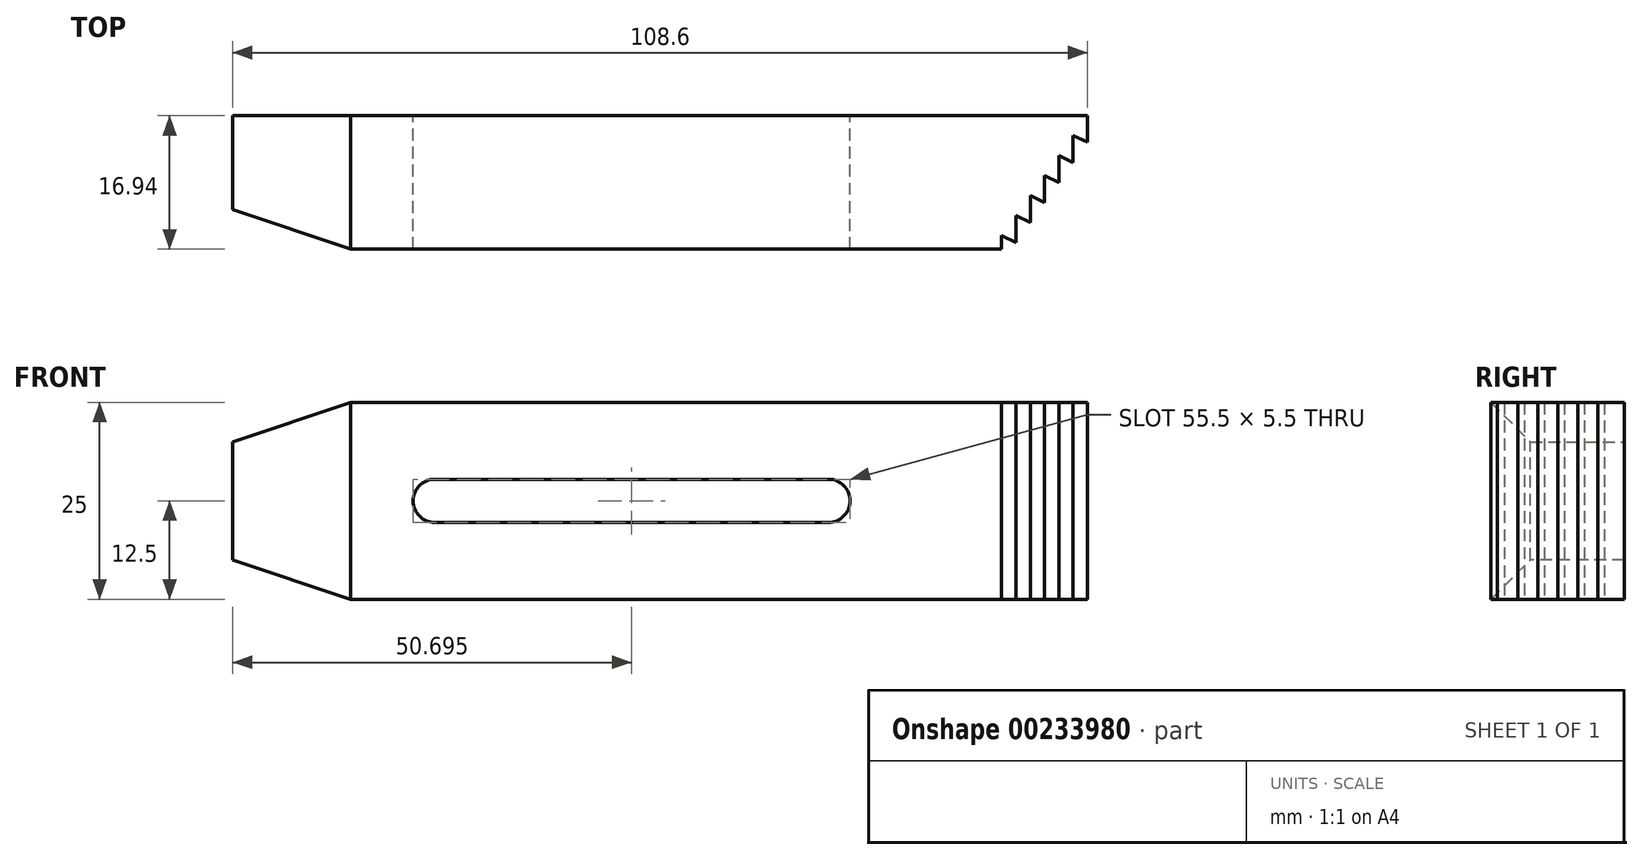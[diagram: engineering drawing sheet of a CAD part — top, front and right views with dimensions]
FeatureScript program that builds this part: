
annotation { "Feature Type Name" : "Feature", "Feature Type Description" : "" }
export const myFeature = defineFeature(function(context is Context, id is Id, definition is map)
    precondition{}
    {
        {
            var Q0;
            Q0=qCreatedBy(makeId("Top.planeOp"),FACE);
            var sketch = newSketch(context, id + "F0", { "sketchPlane" : qUnion([Q0])});
            skLineSegment(sketch, "E0", {"start": v(-54.3, -8.47) * mm, "end": v(-54.3, 8.47) * mm});
            skLineSegment(sketch, "E1", {"start": v(-54.3, -8.47) * mm, "end": v(43.4, -8.47) * mm});
            skLineSegment(sketch, "E2", {"start": v(43.4, -6.78) * mm, "end": v(43.4, -8.47) * mm});
            skLineSegment(sketch, "E3", {"start": v(45.22, -7.63) * mm, "end": v(43.4, -6.78) * mm});
            skLineSegment(sketch, "E4", {"start": v(45.22, -4.24) * mm, "end": v(45.22, -7.63) * mm});
            skLineSegment(sketch, "E5", {"start": v(47.04, -5.09) * mm, "end": v(45.22, -4.24) * mm});
            skLineSegment(sketch, "E6", {"start": v(47.04, -1.7) * mm, "end": v(47.04, -5.09) * mm});
            skLineSegment(sketch, "E7", {"start": v(48.85, -2.54) * mm, "end": v(47.04, -1.7) * mm});
            skLineSegment(sketch, "E8", {"start": v(48.85, 0.85) * mm, "end": v(48.85, -2.54) * mm});
            skLineSegment(sketch, "E9", {"start": v(50.67, 0) * mm, "end": v(48.85, 0.85) * mm});
            skLineSegment(sketch, "E10", {"start": v(50.67, 3.39) * mm, "end": v(50.67, 0) * mm});
            skLineSegment(sketch, "E11", {"start": v(52.48, 2.54) * mm, "end": v(50.67, 3.39) * mm});
            skLineSegment(sketch, "E12", {"start": v(52.48, 5.93) * mm, "end": v(52.48, 2.54) * mm});
            skLineSegment(sketch, "E13", {"start": v(54.3, 5.08) * mm, "end": v(52.48, 5.93) * mm});
            skLineSegment(sketch, "E14", {"start": v(54.3, 8.47) * mm, "end": v(54.3, 5.08) * mm});
            skLineSegment(sketch, "E15", {"start": v(-54.3, 8.47) * mm, "end": v(54.3, 8.47) * mm});
            skSolve(sketch);
        }
        {
            var Q0;
            Q0=makeQuery(id+"F0.imprint","IMPRINT",FACE,{"disambiguationData":[TD([[makeQuery(id+"F0.imprint","IMPRINT",EDGE,{"derivedFrom":sQuery(id+"F0.wireOp",EDGE,"E0")}),-1.0]])]});
            extrude(context, id + "F1", {"entities" : qUnion([Q0]), "depth" : 25 * mm});
        }
        {
            var Q0;
            Q0=makeQuery(id+"F1.opExtrude","SWEPT_FACE",FACE,{"disambiguationData":[OSD([sQuery(id+"F0.wireOp",EDGE,"E15")])]});
            var sketch = newSketch(context, id + "F2", { "sketchPlane" : qUnion([Q0])});
            skArc(sketch, "E16", {"start": v(28.6, 9.75) * mm, "mid": v(31.35, 12.5) * mm, "end": v(28.6, 15.25) * mm});
            skPoint(sketch, "E16.centerSnap0", {"position": v(54.3, 12.5) * mm});
            skArc(sketch, "E17", {"start": v(-21.4, 15.25) * mm, "mid": v(-24.15, 12.5) * mm, "end": v(-21.4, 9.75) * mm});
            skLineSegment(sketch, "E18", {"start": v(28.6, 15.25) * mm, "end": v(-21.4, 15.25) * mm});
            skLineSegment(sketch, "E19", {"start": v(-21.4, 9.75) * mm, "end": v(28.6, 9.75) * mm});
            skSolve(sketch);
        }
        {
            var Q0;
            Q0=makeQuery(id+"F2.imprint","IMPRINT",FACE,{"disambiguationData":[TD([[makeQuery(id+"F2.imprint","IMPRINT",EDGE,{"derivedFrom":sQuery(id+"F2.wireOp",EDGE,"E16")}),1.0]])]});
            var Q1;
            Q1=makeQuery(id+"F1.opExtrude","SWEPT_FACE",FACE,{"disambiguationData":[OSD([sQuery(id+"F0.wireOp",EDGE,"E1")])]});
            extrude(context, id + "F3", {"entities" : qUnion([Q0, Q1]), "operationType" : NewBodyOperationType.REMOVE, "oppositeDirection" : true, "depth" : 25 * mm});
        }
        {
            var Q0;
            Q0=makeQuery(id+"F1.opExtrude","CAP_EDGE",EDGE,{"disambiguationData":[OSD([sQuery(id+"F0.wireOp",EDGE,"E0")])],"isStart":false});
            var Q1;
            Q1=makeQuery(id+"F1.opExtrude","CAP_EDGE",EDGE,{"disambiguationData":[OSD([sQuery(id+"F0.wireOp",EDGE,"E0")])],"isStart":true});
            var Q2;
            Q2=makeQuery(id+"F1.opExtrude","SWEPT_EDGE",EDGE,{"disambiguationData":[OSD([sQuery(id+"F0.wireOp",EDGE,"E0"),sQuery(id+"F0.wireOp",EDGE,"E1")])]});
            chamfer(context, id + "F4", {"entities" : qUnion([Q0, Q1, Q2]), "chamferType" : ChamferType.TWO_OFFSETS, "width1" : 5 * mm, "oppositeDirection" : false, "width2" : 15 * mm});
        }
    });
